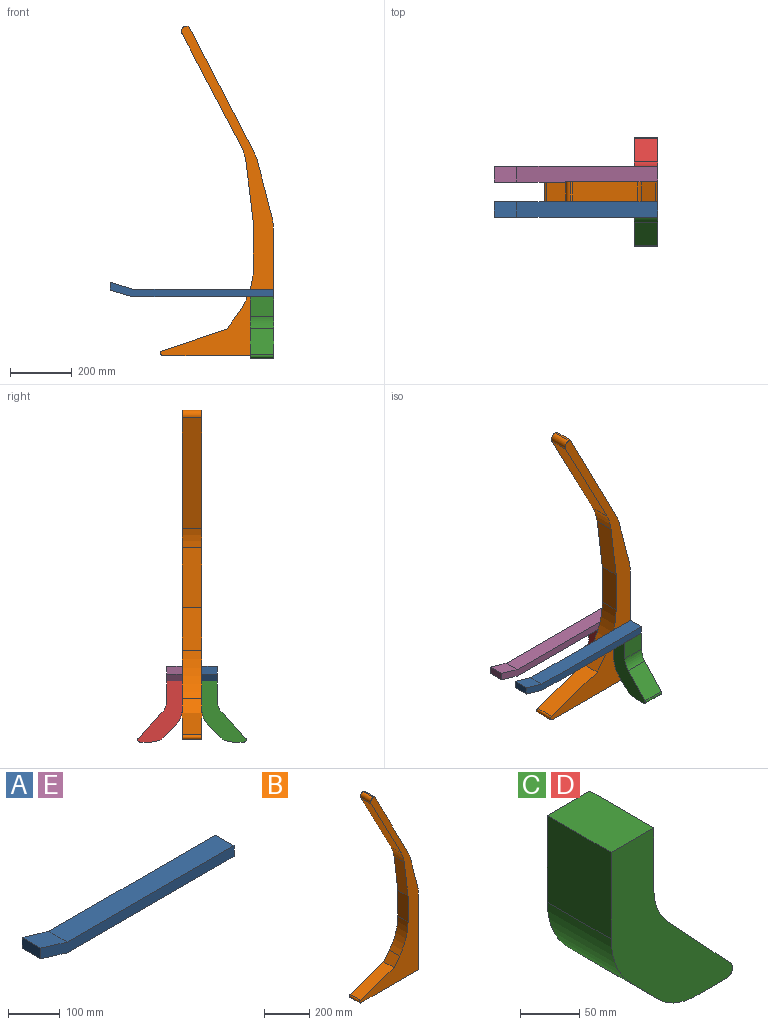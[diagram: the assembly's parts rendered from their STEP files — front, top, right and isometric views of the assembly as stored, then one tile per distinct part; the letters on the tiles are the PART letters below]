
ASSEMBLY  parts=5 mates=4
PART A: 8 faces, bbox 530.2x50.8x47.3 mm
  f0: plane 72.99x50.8mm, normal (0.29,0,0.96), area 3871mm2, adj f1,f5,f6,f7
  f1: plane 50.8x25.4mm, normal (-1,0,0), area 1290.3mm2, adj f0,f2,f6,f7
  f2: plane 72.99x50.8mm, normal (-0.29,0,-0.96), area 3871mm2, adj f1,f3,f6,f7
  f3: plane 457.2x50.8mm, normal (0,0,-1), area 23225.8mm2, adj f2,f4,f6,f7
  f4: plane 50.8x25.4mm, normal (1,0,0), area 1290.3mm2, adj f3,f5,f6,f7
  f5: plane 457.2x50.8mm, normal (0,0,1), area 23225.8mm2, adj f0,f4,f6,f7
  f6: plane 530.19x47.3mm, normal (0,-1,0), area 13466.7mm2, adj f0,f1,f2,f3,f4,f5
  f7: plane 530.19x47.3mm, normal (0,1,0), area 13466.7mm2, adj f0,f1,f2,f3,f4,f5
PART B: 18 faces, bbox 367.5x63.5x1071.2 mm
  f0: cylinder r=181.56mm len=63.5mm, axis (0,1,0), area 2607.9mm2, adj f1,f14,f15,f16
  f1: plane 403.1x208.91mm, normal (0.89,0,0.46), area 28830.4mm2, adj f0,f2,f15,f16
  f2: plane 63.5x6.45mm, normal (0,0,1), area 409.6mm2, adj f1,f15,f16,f17
  f3: plane 359.99x188.81mm, normal (-0.89,0,-0.46), area 25813mm2, adj f4,f15,f16,f17
  f4: cylinder r=181.56mm len=63.5mm, axis (0,1,0), area 4174.2mm2, adj f3,f5,f15,f16
  f5: plane 193.51x63.5mm, normal (-0.99,0,-0.12), area 12378.6mm2, adj f4,f6,f15,f16
  f6: plane 139.39x63.5mm, normal (-1,0,0), area 8851.2mm2, adj f5,f7,f15,f16
  f7: cylinder r=263.63mm len=158.2mm, axis (0,1,0), area 10774mm2, adj f6,f8,f15,f16
  f8: plane 63.5x46.04mm, normal (-0.8,0,0.6), area 3654.4mm2, adj f7,f9,f15,f16
  f9: plane 209.73x71.05mm, normal (-0.32,0,0.95), area 14061mm2, adj f8,f10,f15,f16
  f10: cylinder r=7.68mm len=63.5mm, axis (0,1,0), area 1372.1mm2, adj f9,f11,f15,f16
  f11: plane 359.82x63.5mm, normal (0,0,-1), area 22848.4mm2, adj f10,f12,f15,f16
  f12: plane 406.63x63.5mm, normal (1,0,0), area 25820.7mm2, adj f11,f13,f15,f16
  f13: cylinder r=181.56mm len=63.5mm, axis (0,1,0), area 2904.6mm2, adj f12,f14,f15,f16
  f14: plane 177.96x63.5mm, normal (0.97,0,0.25), area 11668.9mm2, adj f0,f13,f15,f16
  f15: plane 1071.23x367.49mm, normal (0,-1,0), area 77387.3mm2, adj f0,f1,f2,f3,f4,f5,f6,f7
  f16: plane 1071.23x367.49mm, normal (0,1,0), area 77387.3mm2, adj f0,f1,f2,f3,f4,f5,f6,f7
  f17: cylinder r=17.54mm len=63.5mm, axis (0,1,0), area 2287.4mm2, adj f2,f3,f15,f16
PART C: 12 faces, bbox 144.9x76.2x198.6 mm
  f0: plane 76.2x50.8mm, normal (0,0,1), area 3871mm2, adj f1,f9,f10,f11
  f1: plane 89.53x76.2mm, normal (-1,0,0), area 6822.5mm2, adj f0,f2,f10,f11
  f2: cylinder r=81.77mm len=76.2mm, axis (0,1,0), area 4876.8mm2, adj f1,f3,f10,f11
  f3: plane 76.2x32.85mm, normal (-0.71,0,-0.71), area 3530.7mm2, adj f2,f4,f10,f11
  f4: cylinder r=62.92mm len=76.2mm, axis (0,1,0), area 3778.9mm2, adj f3,f5,f10,f11
  f5: plane 76.2x36.41mm, normal (0,0,-1), area 2774.3mm2, adj f4,f6,f10,f11
  f6: cylinder r=7.37mm len=76.2mm, axis (0,1,0), area 1301.4mm2, adj f5,f7,f10,f11
  f7: plane 82.54x76.44mm, normal (0.73,0,0.68), area 8572.3mm2, adj f6,f8,f10,f11
  f8: cylinder r=58.77mm len=76.2mm, axis (0,1,0), area 3345.7mm2, adj f7,f9,f10,f11
  f9: plane 76.2x63.76mm, normal (1,0,0), area 4858.3mm2, adj f0,f8,f10,f11
  f10: plane 198.6x144.86mm, normal (0,-1,0), area 12830.5mm2, adj f0,f1,f2,f3,f4,f5,f6,f7
  f11: plane 198.6x144.86mm, normal (0,1,0), area 12830.5mm2, adj f0,f1,f2,f3,f4,f5,f6,f7
PART D: same geometry as C
PART E: same geometry as A
PLACE A t=(554.6,-866.87,-188.12)mm
PLACE B t=(877.57,-803.37,16.62)mm
PLACE C rot(axis=(0,0,-1),90deg) t=(1030.13,-961.23,-304.32)mm
PLACE D rot(axis=(0,0,1),90deg) t=(953.93,-709.01,-304.32)mm
PLACE E t=(554.6,-752.57,-188.12)mm
MATE fastened A.f3 <-> C.f0  axis (0,0,-1) through (1030.13,-866.87,-217.53)mm
MATE fastened E.f3 <-> D.f0  axis (0,0,-1) through (1030.13,-803.37,-217.53)mm
MATE fastened B.f15 <-> A.f7  axis (0,-1,0) through (1030.13,-866.87,-204.83)mm
MATE fastened E.f6 <-> B.f16  axis (0,-1,0) through (1030.13,-803.37,-204.83)mm
